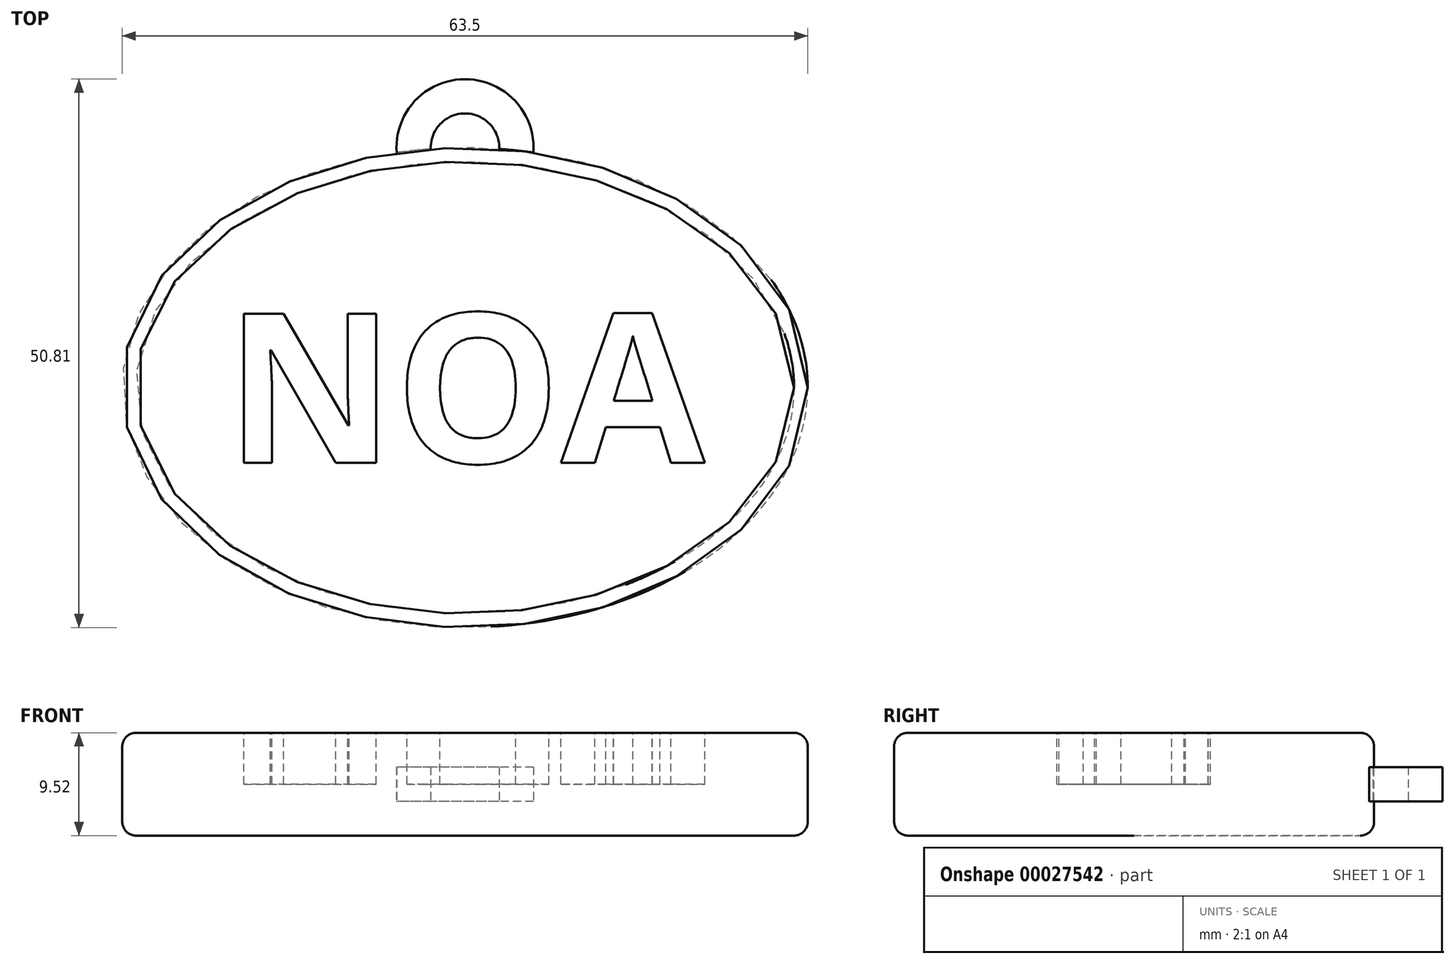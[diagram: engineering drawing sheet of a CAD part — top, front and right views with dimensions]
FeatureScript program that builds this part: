
annotation { "Feature Type Name" : "Feature", "Feature Type Description" : "" }
export const myFeature = defineFeature(function(context is Context, id is Id, definition is map)
    precondition{}
    {
        {
            var Q0;
            Q0=qCreatedBy(makeId("Top.planeOp"),FACE);
            var sketch = newSketch(context, id + "F0", { "sketchPlane" : qUnion([Q0])});
            skEllipse(sketch, "E0", {"center": v(0, 0) * mm, "majorRadius": 31.75 * mm, "minorRadius": 22.23 * mm, "majorAxis": v(1, 0)});
            skSolve(sketch);
        }
        {
            var Q0;
            Q0=makeQuery(id+"F0.imprint","IMPRINT",FACE,{"disambiguationData":[TD([[makeQuery(id+"F0.imprint","IMPRINT",EDGE,{"derivedFrom":sQuery(id+"F0.wireOp",EDGE,"E0")}),1.0]])]});
            extrude(context, id + "F1", {"entities" : qUnion([Q0]), "endBound" : BoundingType.SYMMETRIC, "depth" : 9.52 * mm});
        }
        {
            var Q0;
            Q0=qCreatedBy(makeId("Top.planeOp"),FACE);
            var sketch = newSketch(context, id + "F2", { "sketchPlane" : qUnion([Q0])});
            skCircle(sketch, "E1", {"center": v(0, 22.23) * mm, "radius": 6.35 * mm});
            skCircle(sketch, "E2", {"center": v(0, 22.23) * mm, "radius": 3.18 * mm});
            skSolve(sketch);
        }
        {
            var Q0;
            Q0=makeQuery(id+"F2.imprint","IMPRINT",FACE,{"disambiguationData":[TD([[makeQuery(id+"F2.imprint","IMPRINT",EDGE,{"derivedFrom":sQuery(id+"F2.wireOp",EDGE,"E1")}),1.0]])]});
            extrude(context, id + "F3", {"entities" : qUnion([Q0]), "operationType" : NewBodyOperationType.ADD, "endBound" : BoundingType.SYMMETRIC, "depth" : 3.17 * mm});
        }
        {
            var Q0;
            Q0=makeQuery(id+"F1.opExtrude","CAP_FACE",FACE,{"disambiguationData":[OSD([sQuery(id+"F0.wireOp",EDGE,"E0")])],"isStart":false});
            var sketch = newSketch(context, id + "F4", { "sketchPlane" : qUnion([Q0])});
            skText(sketch, "E3", { "text": "NOA", "fontName": "OpenSans-Bold.ttf"});
            const initialGuessF4  = {"E3": [-0.02222, -0.00696, 1, 0, 0.01392]};
            skSetInitialGuess(sketch, initialGuessF4);
            skSolve(sketch);
        }
        {
            var Q0;
            Q0 = qSketchRegion(id + "F4", true);
            extrude(context, id + "F5", {"entities" : qUnion([Q0]), "operationType" : NewBodyOperationType.REMOVE, "oppositeDirection" : true, "depth" : 4.76 * mm});
        }
        {
            var Q0;
            Q0=makeQuery(id+"F1.opExtrude","CAP_EDGE",EDGE,{"disambiguationData":[OSD([sQuery(id+"F0.wireOp",EDGE,"E0")])],"isStart":false});
            var Q1;
            Q1=makeQuery(id+"F1.opExtrude","CAP_EDGE",EDGE,{"disambiguationData":[OSD([sQuery(id+"F0.wireOp",EDGE,"E0")])],"isStart":true});
            fillet(context, id + "F6", {"entities" : qUnion([Q0, Q1]), "radius" : 1.27 * mm, "tangentPropagation" : true, "allowEdgeOverflow" : false});
        }
    });
